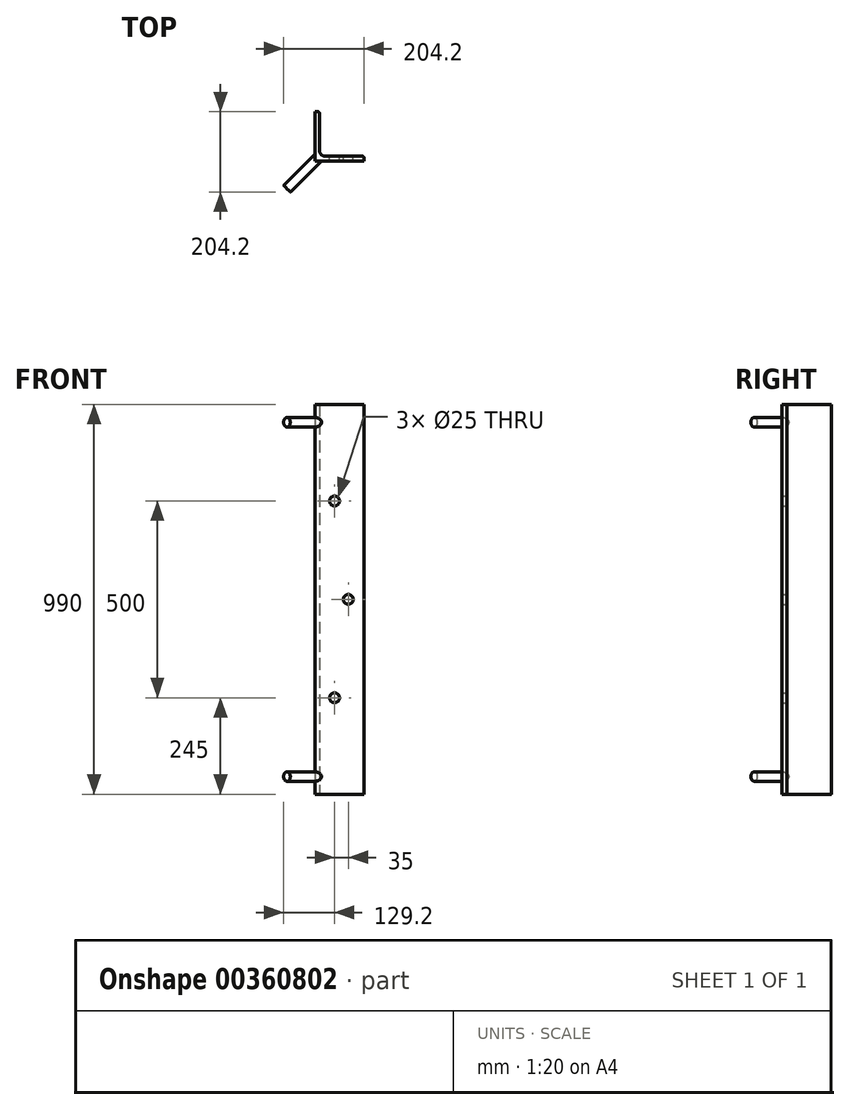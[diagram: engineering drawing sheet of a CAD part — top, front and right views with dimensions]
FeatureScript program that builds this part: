
annotation { "Feature Type Name" : "Feature", "Feature Type Description" : "" }
export const myFeature = defineFeature(function(context is Context, id is Id, definition is map)
    precondition{}
    {
        {
            var Q0;
            Q0=qCreatedBy(makeId("Top.planeOp"),FACE);
            var sketch = newSketch(context, id + "F0", { "sketchPlane" : qUnion([Q0])});
            skLineSegment(sketch, "E0", {"start": v(0, 0) * mm, "end": v(125, 0) * mm});
            skLineSegment(sketch, "E1", {"start": v(125, 0) * mm, "end": v(125, 12) * mm});
            skLineSegment(sketch, "E2", {"start": v(0, 125) * mm, "end": v(12, 125) * mm});
            skLineSegment(sketch, "E3", {"start": v(0, 0) * mm, "end": v(0, 125) * mm});
            skLineSegment(sketch, "E4", {"start": v(12, 125) * mm, "end": v(12, 12) * mm});
            skLineSegment(sketch, "E5", {"start": v(12, 12) * mm, "end": v(125, 12) * mm});
            skSolve(sketch);
        }
        {
            var Q0;
            Q0=makeQuery(id+"F0.imprint","IMPRINT",FACE,{"disambiguationData":[TD([[makeQuery(id+"F0.imprint","IMPRINT",EDGE,{"derivedFrom":sQuery(id+"F0.wireOp",EDGE,"E0")}),1.0]])]});
            extrude(context, id + "F1", {"entities" : qUnion([Q0]), "endBound" : BoundingType.SYMMETRIC, "depth" : 990 * mm});
        }
        {
            var Q0;
            Q0=makeQuery(id+"F1.opExtrude","SWEPT_EDGE",EDGE,{"disambiguationData":[OSD([sQuery(id+"F0.wireOp",EDGE,"E4"),sQuery(id+"F0.wireOp",EDGE,"E5")])]});
            fillet(context, id + "F2", {"entities" : qUnion([Q0]), "radius" : 14 * mm, "tangentPropagation" : true, "allowEdgeOverflow" : false});
        }
        {
            var Q0;
            Q0=makeQuery(id+"F1.opExtrude","SWEPT_EDGE",EDGE,{"disambiguationData":[OSD([sQuery(id+"F0.wireOp",EDGE,"E2"),sQuery(id+"F0.wireOp",EDGE,"E4")])]});
            var Q1;
            Q1=makeQuery(id+"F1.opExtrude","SWEPT_EDGE",EDGE,{"disambiguationData":[OSD([sQuery(id+"F0.wireOp",EDGE,"E1"),sQuery(id+"F0.wireOp",EDGE,"E5")])]});
            fillet(context, id + "F3", {"entities" : qUnion([Q0, Q1]), "radius" : 4.6 * mm, "tangentPropagation" : true, "allowEdgeOverflow" : false});
        }
        {
            var Q0;
            Q0=makeQuery(id+"F1.opExtrude","SWEPT_FACE",FACE,{"disambiguationData":[OSD([sQuery(id+"F0.wireOp",EDGE,"E5")])]});
            var sketch = newSketch(context, id + "F4", { "sketchPlane" : qUnion([Q0])});
            skCircle(sketch, "E6", {"center": v(-85, 0) * mm, "radius": 12.5 * mm});
            skCircle(sketch, "E7", {"center": v(-50, -250) * mm, "radius": 12.5 * mm});
            skCircle(sketch, "E8.MirrorC", {"center": v(-50, 250) * mm, "radius": 12.5 * mm});
            skSolve(sketch);
        }
        {
            var Q0;
            Q0=qCreatedBy(makeId("Front.planeOp"),FACE);
            var Q1;
            Q1=makeQuery(id+"F1.opExtrude","SWEPT_EDGE",EDGE,{"disambiguationData":[OSD([sQuery(id+"F0.wireOp",EDGE,"E0"),sQuery(id+"F0.wireOp",EDGE,"E3")])]});
            cPlane(context, id + "F5", {"entities" : qUnion([Q0, Q1]), "cplaneType" : CPlaneType.LINE_ANGLE, "offset" : 25 * mm, "angle" : 45 * degree, "width" : 150 * mm, "height" : 150 * mm});
        }
        {
            var Q0;
            Q0=qCreatedBy(id+"F5.planeOp",FACE);
            var sketch = newSketch(context, id + "F6", { "sketchPlane" : qUnion([Q0])});
            skCircle(sketch, "E9", {"center": v(0, 450) * mm, "radius": 12 * mm});
            skCircle(sketch, "E10.MirrorC", {"center": v(0, -450) * mm, "radius": 12 * mm});
            skSolve(sketch);
        }
        {
            var Q0;
            Q0=qSketchRegion(id+"F6",true);
            extrude(context, id + "F7", {"entities" : qUnion([Q0]), "operationType" : NewBodyOperationType.ADD, "depth" : 20 * mm, "hasSecondDirection" : true, "secondDirectionOppositeDirection" : true, "secondDirectionDepth" : 100 * mm});
        }
        {
            var Q0;
            Q0=qSketchRegion(id+"F4",true);
            extrude(context, id + "F8", {"entities" : qUnion([Q0]), "operationType" : NewBodyOperationType.REMOVE, "endBound" : BoundingType.THROUGH_ALL, "oppositeDirection" : true, "depth" : 25 * mm});
        }
    });
